# Revit family: Faucet-Lavatory-American_Standard-Studio_S-71058X7_Series
name_source: partatom
category: Plumbing Fixtures
units: mm (PartAtom-declared; Revit-internal decimal feet)

## family parameters
Always vertical = No
Cut with Voids When Loaded = No
OmniClass Number = 23.45.55.17
OmniClass Title = Mixing Faucets
Part Type = Normal
Room Calculation Point = No
Round Connector Dimension = Use Diameter
Shared = Yes
Work Plane-Based = Yes

## types (6) — shared parameters
ADA Compliant = Yes
Assembly Code = D2020300
CW Connection = Yes
CWFU = 1.5
Cold Water Connection Diameter = 3/8"
Cold Water Connection Radius = 3/16"
Default Elevation = 0"
Description = Studio S Widespread Faucet with Lever Handles
HW Connection = Yes
HWFU = 1.5
Height = 5 11/16"
Hot Water Connection Diameter = 0"
Hot Water Connection Radius = 3/16"
Installation Type = Deck Mounted
Length = 7 5/8"
Manufacturer = American Standard
Price = Prices may vary. Please consult Manufacturer Representative for most up-to-date price list.
Product Documentation Link = https://www.americanstandard.ca
Product Page URL = https://www.americanstandard.ca
URL = https://www.americanstandard.ca
Vent Connection = No
WFU = 2
Waste Connection = No

## per-type parameters (varying)
| type | Finish | Knob Handle | Knob Void Height | Lever Handle | Lever Void Height | Material |
| 7105857.002 | Brass-American Standard-002-Polished Chrome | No | 1/2" | Yes | 2 15/16" | Brass-American Standard-002-Polished Chrome |
| 7105857.295 | Brass-American Standard-295-Brushed Nickel | No | 1/2" | Yes | 2 15/16" | Brass-American Standard-295-Brushed Nickel |
| 7105857.243 | Brass-American Standard-243-Matte Black | No | 1/2" | Yes | 2 15/16" | Brass-American Standard-243-Matte Black |
| 7105877.002 | Brass-American Standard-002-Polished Chrome | Yes | 2 15/16" | No | 2 1/8" | Brass-American Standard-002-Polished Chrome |
| 7105877.243 | Brass-American Standard-243-Matte Black | Yes | 2 15/16" | No | 2 1/8" | Brass-American Standard-243-Matte Black |
| 7105877.295 | Brass-American Standard-295-Brushed Nickel | Yes | 2 15/16" | No | 2 1/8" | Brass-American Standard-295-Brushed Nickel |

note: column(s) folded — value = type name in every type: Model

## geometry (parser evidence)
native form markers: Sweep x2
no freeform markers — native parametric forms only
